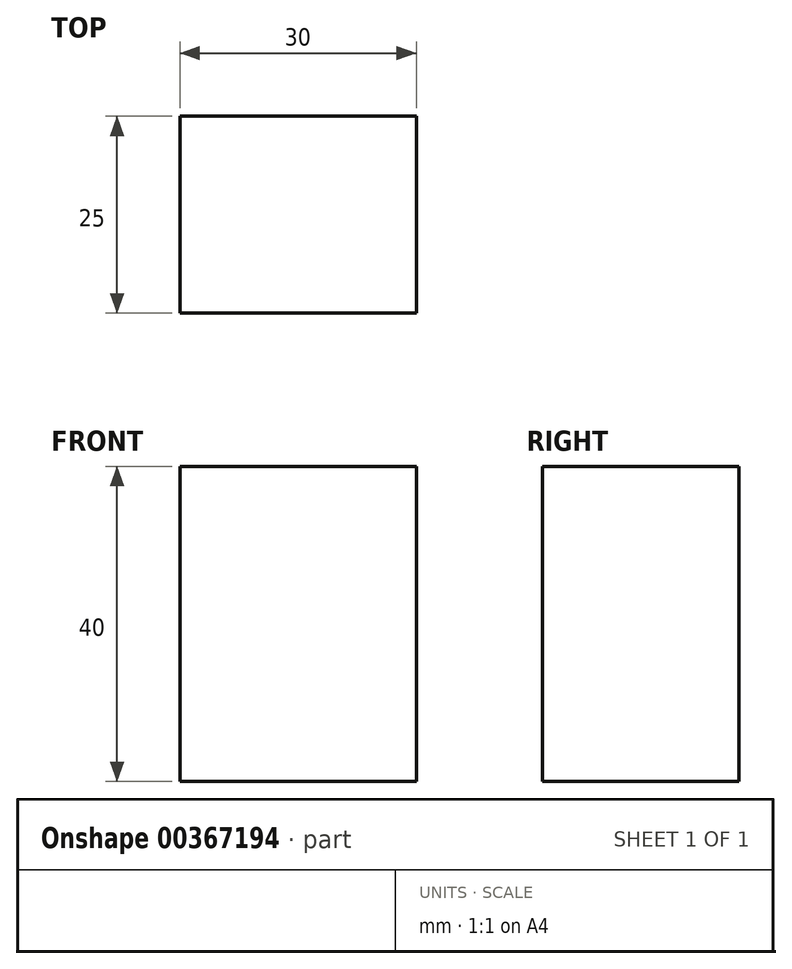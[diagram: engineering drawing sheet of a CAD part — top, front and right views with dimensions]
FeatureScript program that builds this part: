
annotation { "Feature Type Name" : "Feature", "Feature Type Description" : "" }
export const myFeature = defineFeature(function(context is Context, id is Id, definition is map)
    precondition{}
    {
        {
            var Q0;
            Q0=qCreatedBy(makeId("Front.planeOp"),FACE);
            var sketch = newSketch(context, id + "F0", { "sketchPlane" : qUnion([Q0])});
            skLineSegment(sketch, "E0.bottom", {"start": v(0, 0) * mm, "end": v(30, 0) * mm});
            skLineSegment(sketch, "E0.top", {"start": v(0, 40) * mm, "end": v(30, 40) * mm});
            skLineSegment(sketch, "E0.left", {"start": v(0, 0) * mm, "end": v(0, 40) * mm});
            skLineSegment(sketch, "E0.right", {"start": v(30, 0) * mm, "end": v(30, 40) * mm});
            skSolve(sketch);
        }
        {
            var Q0;
            Q0=makeQuery(id+"F0.imprint","IMPRINT",FACE,{"disambiguationData":[TD([[makeQuery(id+"F0.imprint","IMPRINT",EDGE,{"derivedFrom":sQuery(id+"F0.wireOp",EDGE,"E0.bottom")}),1.0]])]});
            extrude(context, id + "F1", {"entities" : qUnion([Q0]), "depth" : 25 * mm});
        }
    });
